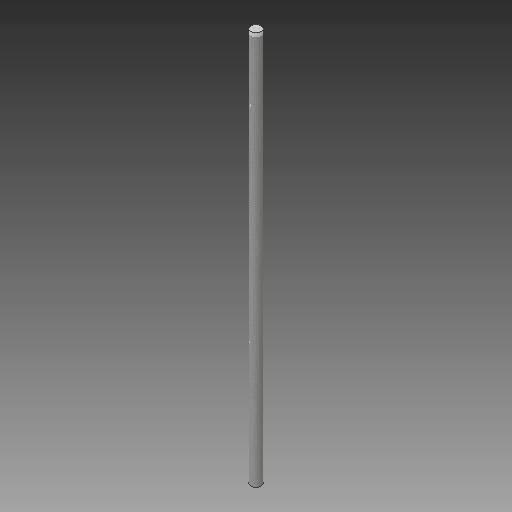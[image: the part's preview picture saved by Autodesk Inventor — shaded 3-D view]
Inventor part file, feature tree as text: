
AUTODESK INVENTOR PART (.ipt)
format: ipt  version: 2018 (Build 220112000, 112)  size: 90,112 bytes
history: native  units: mm
features: extrude x1, thread x1, sketch x1
ambient origin geometry x8: Origin, YZ Plane, XZ Plane, XY Plane, X Axis, Y Axis, Z Axis, Center Point
bodies: Solid1 (feature_tree)
feature tree (3):
  extrude  "Extrusion1"  Depth=530.0mm TaperAngle=0.0deg
  thread  "Thread1"  [1 undecoded]
  sketch  "Sketch1"  dims[d0=14.0mm d1=530.0mm d2=0.0mm d3=530.0mm d4=5.0mm]
note: 1 required parameter value undecoded (feature->parameter linkage not recoverable at this tier; creation-order binding heuristic only, values carry confidence <= 0.55)
